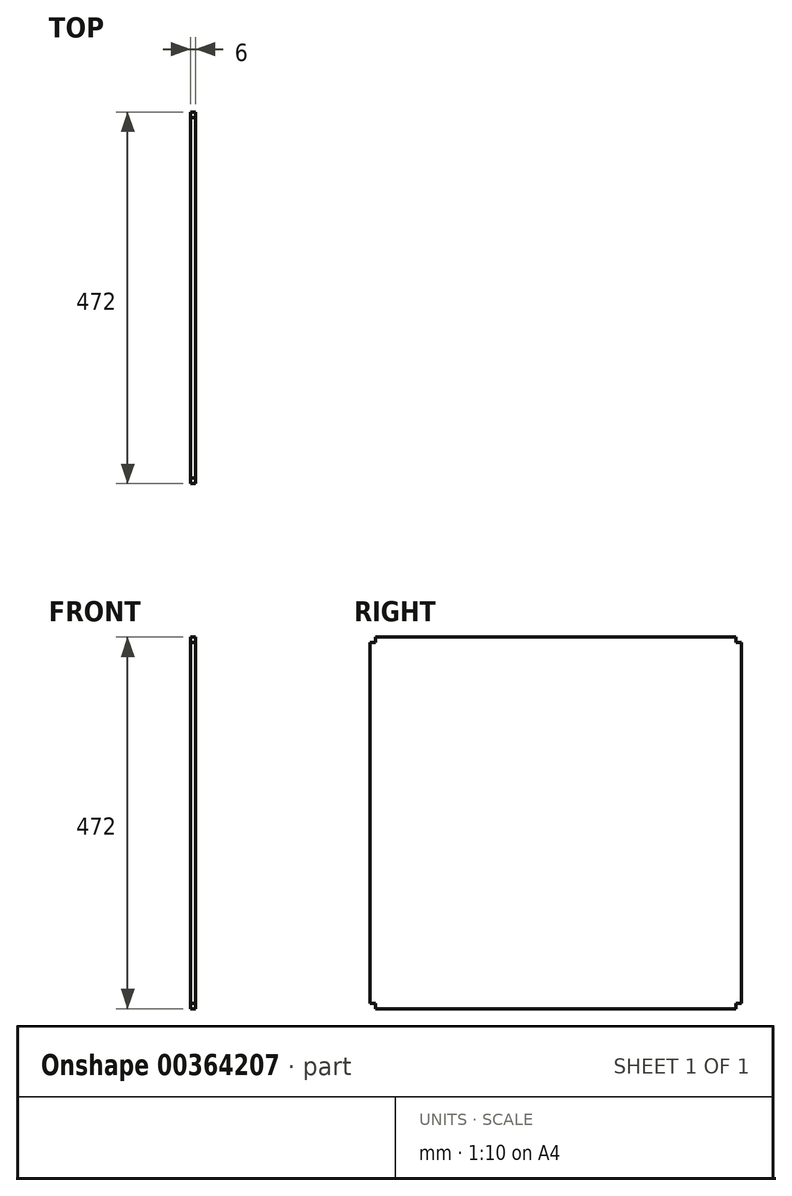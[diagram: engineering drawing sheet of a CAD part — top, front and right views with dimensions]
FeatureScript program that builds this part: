
annotation { "Feature Type Name" : "Feature", "Feature Type Description" : "" }
export const myFeature = defineFeature(function(context is Context, id is Id, definition is map)
    precondition{}
    {
        {
            var Q0;
            Q0=qCreatedBy(makeId("Right.planeOp"),FACE);
            var sketch = newSketch(context, id + "F0", { "sketchPlane" : qUnion([Q0])});
            skLineSegment(sketch, "E0.bottom", {"start": v(229, -236) * mm, "end": v(-229, -236) * mm});
            skLineSegment(sketch, "E0.top", {"start": v(229, 236) * mm, "end": v(-229, 236) * mm});
            skLineSegment(sketch, "E0.left", {"start": v(236, -229) * mm, "end": v(236, 229) * mm});
            skLineSegment(sketch, "E0.right", {"start": v(-236, -229) * mm, "end": v(-236, 229) * mm});
            skPoint(sketch, "E0.middle", {"position": v(0, 0) * mm});
            skPoint(sketch, "E1.orphan", {"position": v(-236, 236) * mm});
            skLineSegment(sketch, "E2.bottom", {"start": v(229, -229) * mm, "end": v(236, -229) * mm});
            skLineSegment(sketch, "E2.left", {"start": v(229, -229) * mm, "end": v(229, -236) * mm});
            skPoint(sketch, "E2.middle", {"position": v(236, -236) * mm});
            skLineSegment(sketch, "E3.bottom", {"start": v(236, 229) * mm, "end": v(229, 229) * mm});
            skLineSegment(sketch, "E3.right", {"start": v(229, 229) * mm, "end": v(229, 236) * mm});
            skPoint(sketch, "E3.middle", {"position": v(236, 236) * mm});
            skLineSegment(sketch, "E4.top", {"start": v(-229, -229) * mm, "end": v(-236, -229) * mm});
            skLineSegment(sketch, "E4.left", {"start": v(-229, -236) * mm, "end": v(-229, -229) * mm});
            skPoint(sketch, "E4.middle", {"position": v(-236, -236) * mm});
            skPoint(sketch, "E3.left.start.orphan", {"position": v(243, 229) * mm});
            skPoint(sketch, "E3.top.end.orphan", {"position": v(229, 243) * mm});
            skPoint(sketch, "E3.top.start.orphan", {"position": v(243, 243) * mm});
            skPoint(sketch, "E2.top.start.orphan", {"position": v(229, -243) * mm});
            skPoint(sketch, "E2.right.end.orphan", {"position": v(243, -243) * mm});
            skPoint(sketch, "E2.right.start.orphan", {"position": v(243, -229) * mm});
            skPoint(sketch, "E4.bottom.start.orphan", {"position": v(-229, -243) * mm});
            skPoint(sketch, "E4.right.end.orphan", {"position": v(-243, -229) * mm});
            skPoint(sketch, "E4.right.start.orphan", {"position": v(-243, -243) * mm});
            skLineSegment(sketch, "E5.bottom", {"start": v(-229, 229) * mm, "end": v(-236, 229) * mm});
            skLineSegment(sketch, "E5.left", {"start": v(-229, 229) * mm, "end": v(-229, 236) * mm});
            skPoint(sketch, "E5.top.start.orphan", {"position": v(-229, 243) * mm});
            skPoint(sketch, "E5.right.end.orphan", {"position": v(-243, 243) * mm});
            skPoint(sketch, "E6.orphan", {"position": v(-243, 229) * mm});
            skSolve(sketch);
        }
        {
            var Q0;
            Q0=makeQuery(id+"F0.imprint","IMPRINT",FACE,{"disambiguationData":[TD([[makeQuery(id+"F0.imprint","IMPRINT",EDGE,{"derivedFrom":sQuery(id+"F0.wireOp",EDGE,"E0.bottom")}),-1.0]])]});
            extrude(context, id + "F1", {"entities" : qUnion([Q0]), "depth" : 6 * mm});
        }
    });
